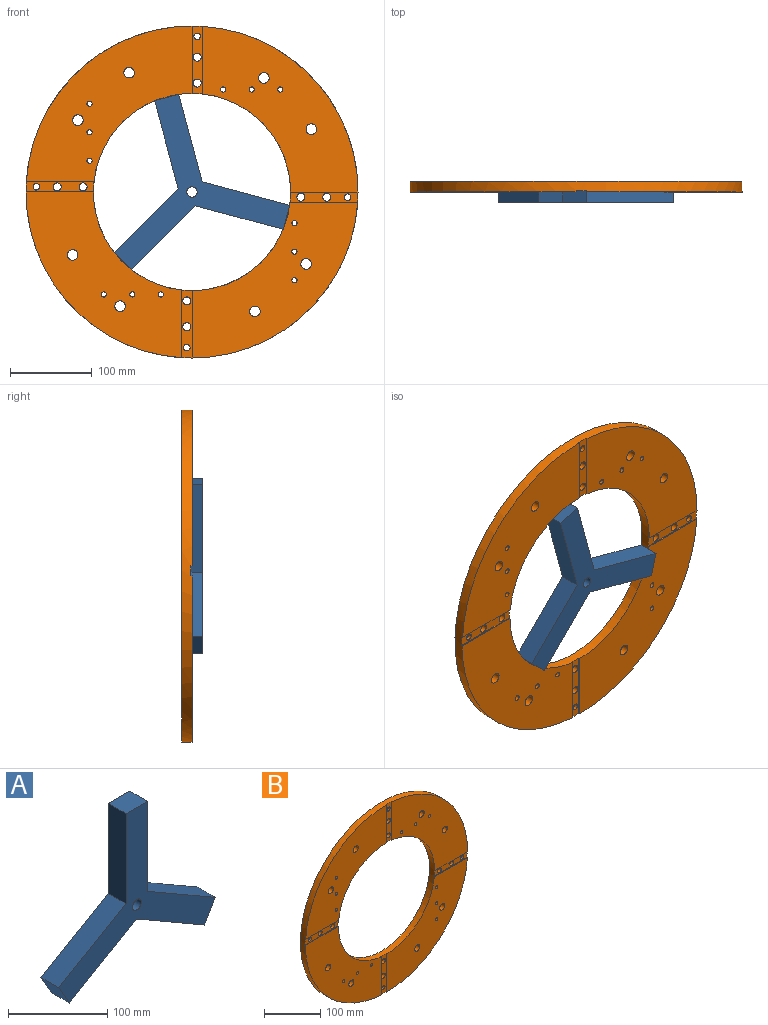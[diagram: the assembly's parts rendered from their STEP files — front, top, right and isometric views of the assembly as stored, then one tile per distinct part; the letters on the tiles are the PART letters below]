
ASSEMBLY  parts=2 mates=1
PART A: 12 faces, bbox 222.5x25.4x192.7 mm
  f0: plane 96.03x55.44mm, normal (-0.5,0,0.87), area 2816.5mm2, adj f1,f8,f10,f11
  f1: plane 26.4x25.4mm, normal (-0.87,0,-0.5), area 774.2mm2, adj f0,f2,f10,f11
  f2: plane 96.03x55.44mm, normal (0.5,0,-0.87), area 2816.5mm2, adj f1,f3,f10,f11
  f3: plane 96.03x55.44mm, normal (-0.5,0,-0.87), area 2816.5mm2, adj f2,f4,f10,f11
  f4: plane 26.4x25.4mm, normal (0.87,0,-0.5), area 774.2mm2, adj f3,f5,f10,f11
  f5: plane 96.03x55.44mm, normal (0.5,0,0.87), area 2816.5mm2, adj f4,f6,f10,f11
  f6: plane 110.88x25.4mm, normal (1,0,0), area 2816.5mm2, adj f5,f7,f10,f11
  f7: plane 30.48x25.4mm, normal (0,0,1), area 774.2mm2, adj f6,f8,f10,f11
  f8: plane 110.88x25.4mm, normal (-1,0,0), area 2816.5mm2, adj f0,f7,f10,f11
  f9: cylinder r=6.35mm len=25.4mm, axis (0,1,0), area 1013.4mm2, adj f10,f11
  f10: plane 222.54x192.72mm, normal (0,-1,0), area 10414.9mm2, adj f0,f1,f2,f3,f4,f5,f6,f7
  f11: plane 222.54x192.72mm, normal (0,1,0), area 10414.9mm2, adj f0,f1,f2,f3,f4,f5,f6,f7
PART B: 67 faces, bbox 406.4x12.7x406.4 mm
  f0: cylinder r=3.17mm len=8.59mm, axis (0,-1,0), area 171.5mm2, adj f14,f66
  f1: cylinder r=3.17mm len=8.59mm, axis (0,-1,0), area 171.5mm2, adj f15,f65
  f2: cylinder r=3.17mm len=8.59mm, axis (0,-1,0), area 171.5mm2, adj f13,f64
  f3: cylinder r=3.17mm len=8.59mm, axis (0,-1,0), area 171.5mm2, adj f13,f63
  f4: cylinder r=3.17mm len=8.59mm, axis (0,-1,0), area 171.5mm2, adj f13,f62
  f5: cylinder r=3.17mm len=8.59mm, axis (0,-1,0), area 171.5mm2, adj f15,f61
  f6: cylinder r=3.17mm len=8.59mm, axis (0,-1,0), area 171.5mm2, adj f15,f60
  f7: cylinder r=3.17mm len=8.59mm, axis (0,-1,0), area 171.5mm2, adj f14,f59
  f8: cylinder r=3.17mm len=8.59mm, axis (0,-1,0), area 171.5mm2, adj f14,f58
  f9: cylinder r=3.17mm len=8.59mm, axis (0,-1,0), area 171.5mm2, adj f16,f57
  f10: cylinder r=3.17mm len=8.59mm, axis (0,-1,0), area 171.5mm2, adj f16,f56
  f11: cylinder r=3.17mm len=8.59mm, axis (0,-1,0), area 171.5mm2, adj f16,f55
  f12: cylinder r=120.65mm len=241.3mm, axis (0,1,0), area 9562.8mm2, adj f13,f14,f15,f16,f18,f19,f20,f21
  f13: plane 202.8x190.5mm, normal (0,-1,0), area 19588.6mm2, adj f2,f3,f4,f12,f17,f20,f28,f39
  f14: plane 202.8x190.5mm, normal (0,-1,0), area 19588.6mm2, adj f0,f7,f8,f12,f17,f25,f29,f40
  f15: plane 202.8x190.5mm, normal (0,-1,0), area 19588.6mm2, adj f1,f5,f6,f12,f17,f22,f26,f42
  f16: plane 202.8x190.5mm, normal (0,-1,0), area 19588.6mm2, adj f9,f10,f11,f12,f17,f19,f23,f44
  f17: cylinder r=203.2mm len=406.4mm, axis (0,1,0), area 16150.1mm2, adj f13,f14,f15,f16,f18,f19,f20,f21
  f18: plane 406.4x406.4mm, normal (0,1,0), area 79380.8mm2, adj f12,f17,f31,f32,f33,f34,f35,f36
  f19: plane 82.55x1.27mm, normal (0,0,1), area 104.8mm2, adj f12,f16,f17,f21
  f20: plane 82.82x1.27mm, normal (0,0,-1), area 105.2mm2, adj f12,f13,f17,f21
  f21: plane 83.22x12.7mm, normal (0,-1,0), area 849.8mm2, adj f12,f17,f19,f20,f37,f38,f53
  f22: plane 82.55x1.27mm, normal (-1,0,0), area 104.8mm2, adj f12,f15,f17,f24
  f23: plane 82.82x1.27mm, normal (1,0,0), area 105.2mm2, adj f12,f16,f17,f24
  f24: plane 83.22x12.7mm, normal (0,-1,0), area 849.8mm2, adj f12,f17,f22,f23,f35,f36,f51
  f25: plane 82.55x1.27mm, normal (0,0,-1), area 104.8mm2, adj f12,f14,f17,f27
  f26: plane 82.82x1.27mm, normal (0,0,1), area 105.2mm2, adj f12,f15,f17,f27
  f27: plane 83.22x12.7mm, normal (0,-1,0), area 849.8mm2, adj f12,f17,f25,f26,f33,f34,f49
  f28: plane 82.55x1.27mm, normal (1,0,0), area 104.8mm2, adj f12,f13,f17,f30
  f29: plane 82.82x1.27mm, normal (-1,0,0), area 105.2mm2, adj f12,f14,f17,f30
  f30: plane 83.22x12.7mm, normal (0,-1,0), area 849.8mm2, adj f12,f17,f28,f29,f31,f32,f47
  f31: cylinder r=4.89mm len=11.43mm, axis (0,-1,0), area 351.1mm2, adj f18,f30
  f32: cylinder r=4.89mm len=11.43mm, axis (0,-1,0), area 351.1mm2, adj f18,f30
  f33: cylinder r=4.89mm len=11.43mm, axis (0,-1,0), area 351.1mm2, adj f18,f27
  f34: cylinder r=4.89mm len=11.43mm, axis (0,-1,0), area 351.1mm2, adj f18,f27
  f35: cylinder r=4.89mm len=11.43mm, axis (0,-1,0), area 351.1mm2, adj f18,f24
  f36: cylinder r=4.89mm len=11.43mm, axis (0,-1,0), area 351.1mm2, adj f18,f24
  f37: cylinder r=4.89mm len=11.43mm, axis (0,-1,0), area 351.1mm2, adj f18,f21
  f38: cylinder r=4.89mm len=11.43mm, axis (0,-1,0), area 351.1mm2, adj f18,f21
  f39: cylinder r=6.48mm len=12.95mm, axis (0,-1,0), area 516.8mm2, adj f13,f18
  f40: cylinder r=6.48mm len=12.95mm, axis (0,-1,0), area 516.8mm2, adj f14,f18
  f41: cylinder r=6.48mm len=12.95mm, axis (0,-1,0), area 516.8mm2, adj f14,f18
  f42: cylinder r=6.48mm len=12.95mm, axis (0,-1,0), area 516.8mm2, adj f15,f18
  f43: cylinder r=6.48mm len=12.95mm, axis (0,-1,0), area 516.8mm2, adj f15,f18
  f44: cylinder r=6.48mm len=12.95mm, axis (0,-1,0), area 516.8mm2, adj f16,f18
  f45: cylinder r=6.48mm len=12.95mm, axis (0,-1,0), area 516.8mm2, adj f16,f18
  f46: cylinder r=6.48mm len=12.95mm, axis (0,-1,0), area 516.8mm2, adj f13,f18
  f47: cylinder r=3.97mm len=7.94mm, axis (0,1,0), area 114.3mm2, adj f30,f48
  f48: cone r=3.97mm half-angle=41deg, axis (0,1,0), area 395.7mm2, adj f18,f47
  f49: cylinder r=3.97mm len=7.94mm, axis (0,1,0), area 114.3mm2, adj f27,f50
  f50: cone r=3.97mm half-angle=41deg, axis (0,1,0), area 395.7mm2, adj f18,f49
  f51: cylinder r=3.97mm len=7.94mm, axis (0,1,0), area 114.3mm2, adj f24,f52
  f52: cone r=3.97mm half-angle=41deg, axis (0,1,0), area 395.7mm2, adj f18,f51
  f53: cylinder r=3.97mm len=7.94mm, axis (0,1,0), area 114.3mm2, adj f21,f54
  f54: cone r=3.97mm half-angle=41deg, axis (0,1,0), area 395.7mm2, adj f18,f53
  f55: cone r=2.55mm half-angle=41deg, axis (0,1,0), area 169.5mm2, adj f11,f18
  f56: cone r=2.55mm half-angle=41deg, axis (0,1,0), area 169.5mm2, adj f10,f18
  f57: cone r=2.55mm half-angle=41deg, axis (0,1,0), area 169.5mm2, adj f9,f18
  f58: cone r=2.55mm half-angle=41deg, axis (0,1,0), area 169.5mm2, adj f8,f18
  f59: cone r=2.55mm half-angle=41deg, axis (0,1,0), area 169.5mm2, adj f7,f18
  f60: cone r=2.55mm half-angle=41deg, axis (0,1,0), area 169.5mm2, adj f6,f18
  f61: cone r=2.55mm half-angle=41deg, axis (0,1,0), area 169.5mm2, adj f5,f18
  f62: cone r=2.55mm half-angle=41deg, axis (0,1,0), area 169.5mm2, adj f4,f18
  f63: cone r=2.55mm half-angle=41deg, axis (0,1,0), area 169.5mm2, adj f3,f18
  f64: cone r=2.55mm half-angle=41deg, axis (0,1,0), area 169.5mm2, adj f2,f18
  f65: cone r=2.55mm half-angle=41deg, axis (0,1,0), area 169.5mm2, adj f1,f18
  f66: cone r=2.55mm half-angle=41deg, axis (0,1,0), area 169.5mm2, adj f0,f18
PLACE A rot(axis=(0,-1,0),15deg) t=(14.73,0,2.91)mm
PLACE B t=(14.73,0,2.91)mm
MATE revolute A.f9 <-> B.f12  axis (0,1,0) through (14.73,0,2.91)mm
